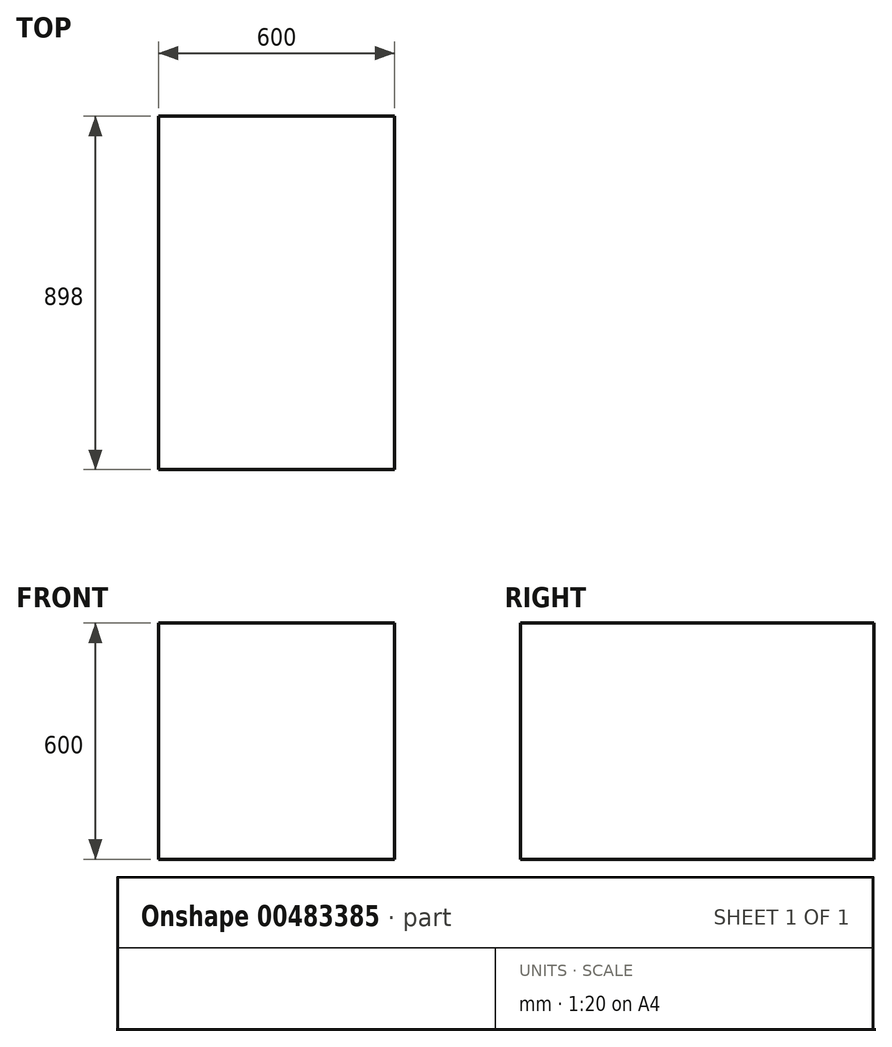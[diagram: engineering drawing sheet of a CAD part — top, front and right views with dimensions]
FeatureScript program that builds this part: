
annotation { "Feature Type Name" : "Feature", "Feature Type Description" : "" }
export const myFeature = defineFeature(function(context is Context, id is Id, definition is map)
    precondition{}
    {
        {
            var Q0;
            Q0=qCreatedBy(makeId("Top.planeOp"),FACE);
            var sketch = newSketch(context, id + "F0", { "sketchPlane" : qUnion([Q0])});
            skLineSegment(sketch, "E0.bottom", {"start": v(-523.32, -49.2) * mm, "end": v(76.68, -49.2) * mm});
            skLineSegment(sketch, "E0.top", {"start": v(-523.32, -947.2) * mm, "end": v(76.68, -947.2) * mm});
            skLineSegment(sketch, "E0.left", {"start": v(-523.32, -49.2) * mm, "end": v(-523.32, -947.2) * mm});
            skLineSegment(sketch, "E0.right", {"start": v(76.68, -49.2) * mm, "end": v(76.68, -947.2) * mm});
            skSolve(sketch);
        }
        {
            var Q0;
            Q0=makeQuery(id+"F0.imprint","IMPRINT",FACE,{"disambiguationData":[TD([[makeQuery(id+"F0.imprint","IMPRINT",EDGE,{"derivedFrom":sQuery(id+"F0.wireOp",EDGE,"E0.bottom")}),-1.0]])]});
            extrude(context, id + "F1", {"entities" : qUnion([Q0]), "depth" : 600 * mm});
        }
    });
